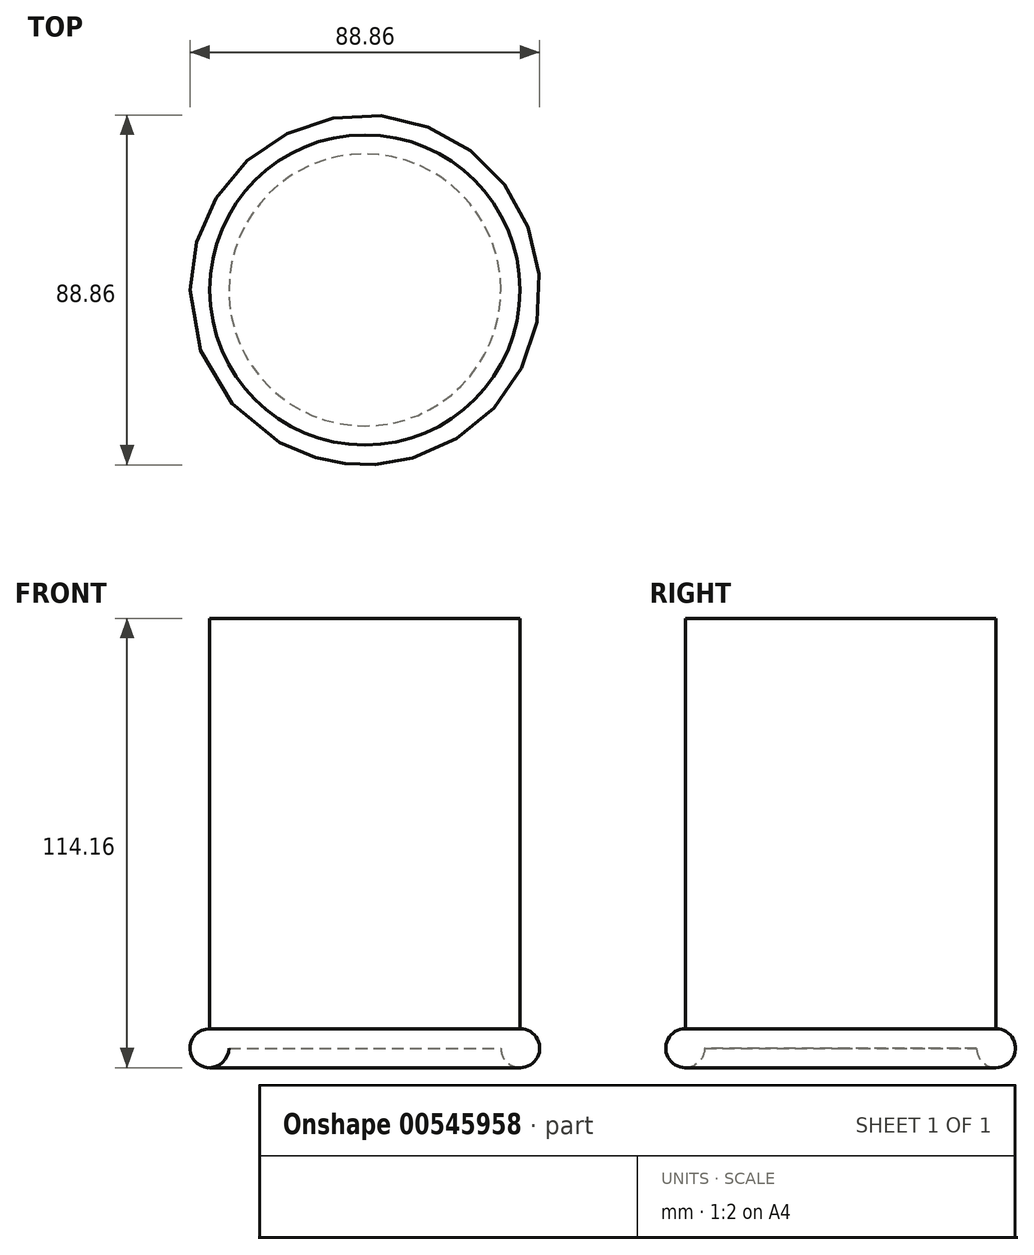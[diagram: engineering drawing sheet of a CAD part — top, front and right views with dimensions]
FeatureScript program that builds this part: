
annotation { "Feature Type Name" : "Feature", "Feature Type Description" : "" }
export const myFeature = defineFeature(function(context is Context, id is Id, definition is map)
    precondition{}
    {
        {
            var Q0;
            Q0=qCreatedBy(makeId("Top.planeOp"),FACE);
            var sketch = newSketch(context, id + "F0", { "sketchPlane" : qUnion([Q0])});
            skCircle(sketch, "E0", {"center": v(0, 0) * mm, "radius": 39.4 * mm});
            skSolve(sketch);
        }
        {
            var Q0;
            Q0=makeQuery(id+"F0.imprint","IMPRINT",FACE,{"disambiguationData":[TD([[makeQuery(id+"F0.imprint","IMPRINT",EDGE,{"derivedFrom":sQuery(id+"F0.wireOp",EDGE,"E0")}),1.0]])]});
            extrude(context, id + "F1", {"entities" : qUnion([Q0]), "depth" : 109.22 * mm, "offsetDistance" : 25.4 * mm});
        }
        {
            var Q0;
            Q0=qCreatedBy(makeId("Front.planeOp"),FACE);
            var sketch = newSketch(context, id + "F2", { "sketchPlane" : qUnion([Q0])});
            skCircle(sketch, "E1", {"center": v(-39.5, 0) * mm, "radius": 4.94 * mm});
            skSolve(sketch);
        }
        {
            var Q0;
            Q0=qCreatedBy(makeId("Right.planeOp"),FACE);
            var sketch = newSketch(context, id + "F3", { "sketchPlane" : qUnion([Q0])});
            skLineSegment(sketch, "E2", {"start": v(0, 0) * mm, "end": v(0, -69.2) * mm});
            skSolve(sketch);
        }
        {
            var Q0;
            Q0=makeQuery(id+"F2.imprint","IMPRINT",FACE,{"disambiguationData":[TD([[makeQuery(id+"F2.imprint","IMPRINT",EDGE,{"derivedFrom":sQuery(id+"F2.wireOp",EDGE,"E1")}),1.0]])]});
            var Q1;
            Q1=sQuery(id+"F3.wireOp",EDGE,"E2");
            revolve(context, id + "F4", {"operationType" : NewBodyOperationType.ADD, "entities" : qUnion([Q0]), "axis" : qUnion([Q1]), "revolveType" : RevolveType.FULL});
        }
    });
